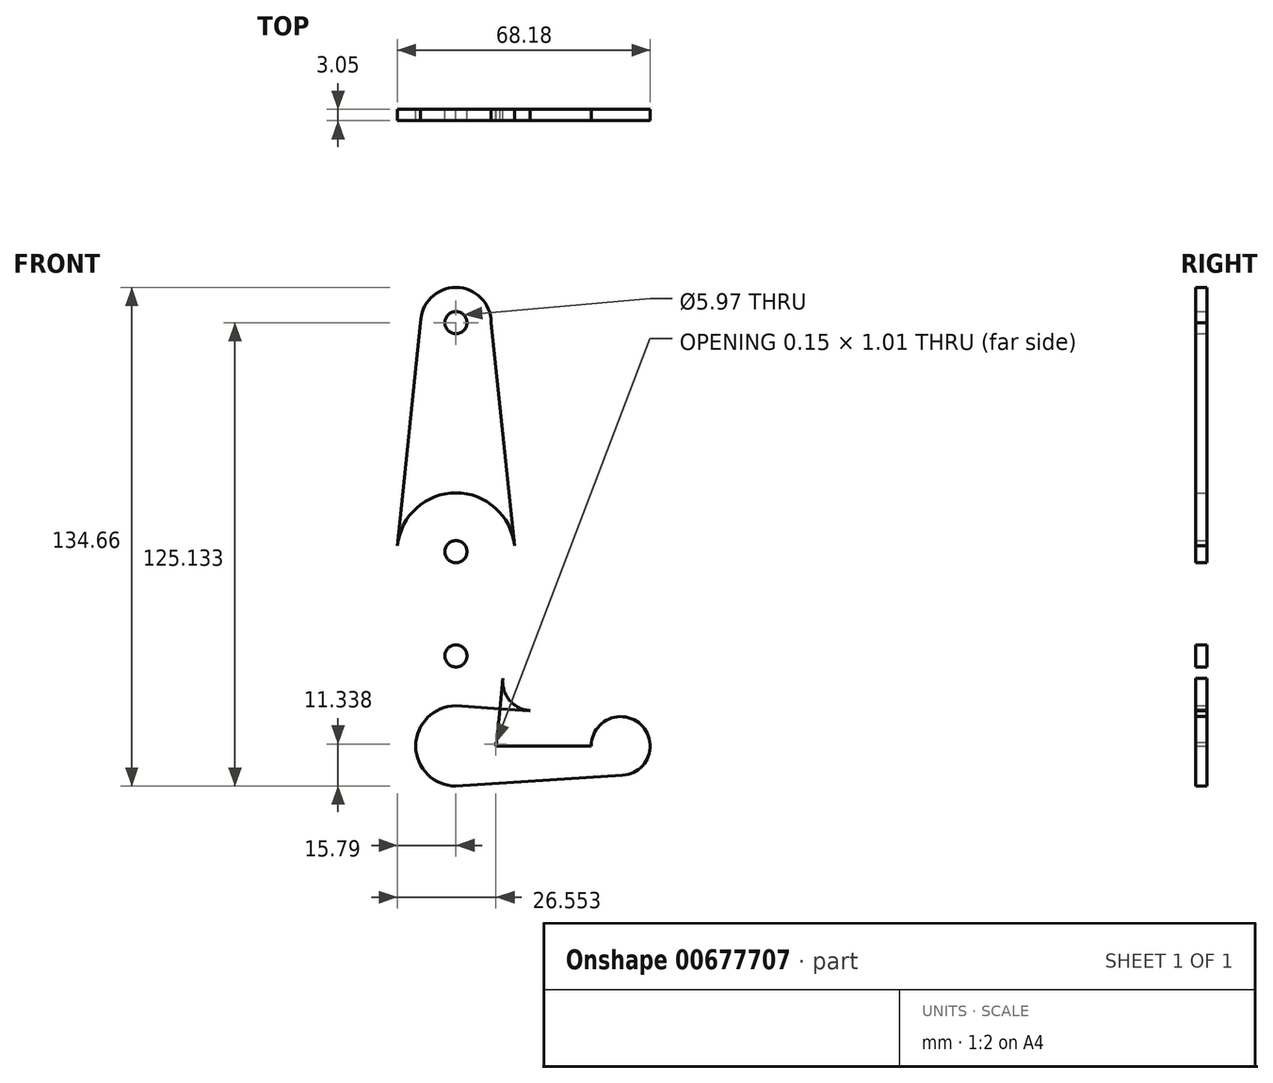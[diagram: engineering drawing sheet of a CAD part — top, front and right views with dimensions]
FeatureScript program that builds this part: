
annotation { "Feature Type Name" : "Feature", "Feature Type Description" : "" }
export const myFeature = defineFeature(function(context is Context, id is Id, definition is map)
    precondition{}
    {
        {
            var Q0;
            Q0=qCreatedBy(makeId("Front.planeOp"),FACE);
            var sketch = newSketch(context, id + "F0", { "sketchPlane" : qUnion([Q0])});
            skLineSegment(sketch, "E0", {"start": v(0, 61.82) * mm, "end": v(0, -52.48) * mm});
            skLineSegment(sketch, "E1", {"start": v(0, -52.48) * mm, "end": v(0, 11.02) * mm});
            skPoint(sketch, "E2.end.orphan", {"position": v(54.75, -52.48) * mm});
            skPoint(sketch, "E3.orphan", {"position": v(35.11, -52.48) * mm});
            skPoint(sketch, "E4.end.orphan", {"position": v(17.56, -52.48) * mm});
            skLineSegment(sketch, "E5", {"start": v(0, -52.48) * mm, "end": v(44.45, -52.48) * mm});
            skCircle(sketch, "E6", {"center": v(0, 0) * mm, "radius": 15.88 * mm});
            skCircle(sketch, "E7", {"center": v(0, 61.82) * mm, "radius": 9.53 * mm});
            skCircle(sketch, "E8", {"center": v(44.45, -52.48) * mm, "radius": 7.94 * mm});
            skCircle(sketch, "E9", {"center": v(0, -52.48) * mm, "radius": 10.84 * mm});
            skLineSegment(sketch, "E10", {"start": v(-15.96, 0) * mm, "end": v(-15.79, -1.66) * mm});
            skLineSegment(sketch, "E11", {"start": v(0, -41.64) * mm, "end": v(44.96, -44.56) * mm});
            skLineSegment(sketch, "E12", {"start": v(0, -63.31) * mm, "end": v(44.96, -60.4) * mm});
            skLineSegment(sketch, "E13", {"start": v(0, 61.82) * mm, "end": v(-9.53, 61.82) * mm});
            skLineSegment(sketch, "E14", {"start": v(-9.53, 61.82) * mm, "end": v(-15.79, 1.64) * mm});
            skLineSegment(sketch, "E15.trimOffspring", {"start": v(10.8, -51.47) * mm, "end": v(10.69, -52.48) * mm});
            skPoint(sketch, "E16.trimOffspring.end.orphan", {"position": v(10.69, -50.69) * mm});
            skLineSegment(sketch, "E17", {"start": v(9.53, 61.82) * mm, "end": v(15.79, 1.64) * mm});
            skPoint(sketch, "E18.trimOffspring.end.orphan", {"position": v(10.8, -49.71) * mm});
            skPoint(sketch, "E19.end.orphan", {"position": v(17.76, 0) * mm});
            skLineSegment(sketch, "E20", {"start": v(15.88, 0) * mm, "end": v(10.89, -52.48) * mm});
            skLineSegment(sketch, "E21", {"start": v(-15.96, 0) * mm, "end": v(-10.65, -50.46) * mm});
            skCircle(sketch, "E22", {"center": v(0, 40.81) * mm, "radius": 2.98 * mm});
            skCircle(sketch, "E23", {"center": v(0, 0) * mm, "radius": 2.98 * mm});
            skCircle(sketch, "E24", {"center": v(0, 61.82) * mm, "radius": 2.98 * mm});
            skCircle(sketch, "E25", {"center": v(0, -28.15) * mm, "radius": 2.98 * mm});
            skLineSegment(sketch, "E26", {"start": v(44.96, -44.56) * mm, "end": v(20.02, -42.94) * mm});
            skLineSegment(sketch, "E27", {"start": v(12.62, -34.25) * mm, "end": v(15.88, 0) * mm});
            skPoint(sketch, "E28.visualSharp", {"position": v(11.84, -42.4) * mm});
            skArc(sketch, "E28.filletArc", {"start": v(12.62, -34.25) * mm, "mid": v(14.48, -40.16) * mm, "end": v(20.02, -42.94) * mm});
            skSolve(sketch);
        }
        {
            var Q0;
            {var subQ0=sQuery(id+"F0.wireOp",EDGE,"E27");var subQ1=sQuery(id+"F0.wireOp",EDGE,"E6");var subQ2=makeQuery(id+"F0.imprint","INTERSECT",VERTEX,{"disambiguationData":[OD(0.0)],"derivedFrom":[subQ1,subQ0]});Q0=makeQuery(id+"F0.imprint","IMPRINT",FACE,{"disambiguationData":[TD([[makeQuery(id+"F0.imprint","IMPRINT",EDGE,{"disambiguationData":[TD([[subQ2,1.0]])],"derivedFrom":subQ1}),1.0]])]});}
            var Q1;
            {var subQ0=sQuery(id+"F0.wireOp",EDGE,"E12");var subQ1=sQuery(id+"F0.wireOp",EDGE,"E9");var subQ2=makeQuery(id+"F0.imprint","INTERSECT",VERTEX,{"disambiguationData":[OD(0.0)],"derivedFrom":[subQ1,subQ0]});Q1=makeQuery(id+"F0.imprint","IMPRINT",FACE,{"disambiguationData":[TD([[makeQuery(id+"F0.imprint","IMPRINT",EDGE,{"disambiguationData":[TD([[subQ2,-1.0]])],"derivedFrom":subQ1}),1.0]])]});}
            var Q2;
            {var subQ0=sQuery(id+"F0.wireOp",EDGE,"E8");var subQ1=makeQuery(id+"F0.imprint","INTERSECT",VERTEX,{"derivedFrom":[subQ0,sQuery(id+"F0.wireOp",EDGE,"E26")]});Q2=makeQuery(id+"F0.imprint","IMPRINT",FACE,{"disambiguationData":[TD([[makeQuery(id+"F0.imprint","IMPRINT",EDGE,{"disambiguationData":[TD([[subQ1,-1.0]])],"derivedFrom":subQ0}),1.0]])]});}
            var Q3;
            {var subQ0=sQuery(id+"F0.wireOp",EDGE,"E28.filletArc");Q3=makeQuery(id+"F0.imprint","IMPRINT",FACE,{"disambiguationData":[TD([[makeQuery(id+"F0.imprint","IMPRINT",EDGE,{"derivedFrom":subQ0}),-1.0]])]});}
            var Q4;
            {var subQ3=sQuery(id+"F0.wireOp",EDGE,"E24");var subQ6=sQuery(id+"F0.wireOp",EDGE,"E0");var subQ8=makeQuery(id+"F0.imprint","INTERSECT",VERTEX,{"derivedFrom":[subQ6,subQ3]});Q4=makeQuery(id+"F0.imprint","IMPRINT",FACE,{"disambiguationData":[TD([[makeQuery(id+"F0.imprint","IMPRINT",EDGE,{"disambiguationData":[TD([[subQ8,-1.0]])],"derivedFrom":subQ6}),1.0]])]});}
            var Q5;
            {var subQ0=sQuery(id+"F0.wireOp",EDGE,"E24");var subQ1=sQuery(id+"F0.wireOp",EDGE,"E0");var subQ2=makeQuery(id+"F0.imprint","INTERSECT",VERTEX,{"derivedFrom":[subQ1,subQ0]});Q5=makeQuery(id+"F0.imprint","IMPRINT",FACE,{"disambiguationData":[TD([[makeQuery(id+"F0.imprint","IMPRINT",EDGE,{"disambiguationData":[TD([[subQ2,-1.0]])],"derivedFrom":subQ1}),-1.0]])]});}
            var Q6;
            {var subQ0=sQuery(id+"F0.wireOp",EDGE,"E17");Q6=makeQuery(id+"F0.imprint","IMPRINT",FACE,{"disambiguationData":[TD([[makeQuery(id+"F0.imprint","IMPRINT",EDGE,{"derivedFrom":subQ0}),-1.0]])]});}
            var Q7;
            {var subQ0=sQuery(id+"F0.wireOp",EDGE,"E14");Q7=makeQuery(id+"F0.imprint","IMPRINT",FACE,{"disambiguationData":[TD([[makeQuery(id+"F0.imprint","IMPRINT",EDGE,{"derivedFrom":subQ0}),1.0]])]});}
            var Q8;
            {var subQ2=sQuery(id+"F0.wireOp",EDGE,"E0");var subQ5=sQuery(id+"F0.wireOp",EDGE,"E1");var subQ8=makeQuery(id+"F0.imprint","INTERSECT",VERTEX,{"derivedFrom":[subQ2,subQ5]});Q8=makeQuery(id+"F0.imprint","IMPRINT",FACE,{"disambiguationData":[TD([[makeQuery(id+"F0.imprint","IMPRINT",EDGE,{"disambiguationData":[TD([[subQ8,1.0]])],"derivedFrom":subQ2}),-1.0]])]});}
            var Q9;
            {var subQ1=sQuery(id+"F0.wireOp",EDGE,"E1");var subQ8=sQuery(id+"F0.wireOp",EDGE,"E25");var subQ9=makeQuery(id+"F0.imprint","INTERSECT",VERTEX,{"disambiguationData":[OD(1.0)],"derivedFrom":[subQ1,subQ8]});Q9=makeQuery(id+"F0.imprint","IMPRINT",FACE,{"disambiguationData":[TD([[makeQuery(id+"F0.imprint","IMPRINT",EDGE,{"disambiguationData":[TD([[subQ9,-1.0]])],"derivedFrom":subQ1}),1.0]])]});}
            var Q10;
            {var subQ3=sQuery(id+"F0.wireOp",EDGE,"E5");var subQ8=makeQuery(id+"F0.imprint","INTERSECT",VERTEX,{"derivedFrom":[subQ3,sQuery(id+"F0.wireOp",EDGE,"E20")]});Q10=makeQuery(id+"F0.imprint","IMPRINT",FACE,{"disambiguationData":[TD([[makeQuery(id+"F0.imprint","IMPRINT",EDGE,{"disambiguationData":[TD([[subQ8,1.0]])],"derivedFrom":subQ3}),-1.0]])]});}
            var Q11;
            {var subQ4=sQuery(id+"F0.wireOp",EDGE,"E1");var subQ5=sQuery(id+"F0.wireOp",EDGE,"E0");var subQ6=makeQuery(id+"F0.imprint","INTERSECT",VERTEX,{"derivedFrom":[subQ5,subQ4]});Q11=makeQuery(id+"F0.imprint","IMPRINT",FACE,{"disambiguationData":[TD([[makeQuery(id+"F0.imprint","IMPRINT",EDGE,{"disambiguationData":[TD([[subQ6,1.0]])],"derivedFrom":subQ5}),1.0]])]});}
            var Q12;
            {var subQ0=sQuery(id+"F0.wireOp",EDGE,"E5");var subQ6=sQuery(id+"F0.wireOp",EDGE,"E1");var subQ9=makeQuery(id+"F0.imprint","INTERSECT",VERTEX,{"derivedFrom":[subQ6,subQ0]});Q12=makeQuery(id+"F0.imprint","IMPRINT",FACE,{"disambiguationData":[TD([[makeQuery(id+"F0.imprint","IMPRINT",EDGE,{"disambiguationData":[TD([[subQ9,-1.0]])],"derivedFrom":subQ0}),-1.0]])]});}
            var Q13;
            {var subQ5=sQuery(id+"F0.wireOp",EDGE,"E26");Q13=makeQuery(id+"F0.imprint","IMPRINT",FACE,{"disambiguationData":[TD([[makeQuery(id+"F0.imprint","IMPRINT",EDGE,{"derivedFrom":subQ5}),1.0]])]});}
            var Q14;
            {var subQ3=sQuery(id+"F0.wireOp",EDGE,"E20");var subQ6=sQuery(id+"F0.wireOp",EDGE,"E5");var subQ8=makeQuery(id+"F0.imprint","INTERSECT",VERTEX,{"derivedFrom":[subQ6,subQ3]});Q14=makeQuery(id+"F0.imprint","IMPRINT",FACE,{"disambiguationData":[TD([[makeQuery(id+"F0.imprint","IMPRINT",EDGE,{"disambiguationData":[TD([[subQ8,1.0]])],"derivedFrom":subQ6}),1.0]])]});}
            var Q15;
            {var subQ7=sQuery(id+"F0.wireOp",EDGE,"E15.trimOffspring");Q15=makeQuery(id+"F0.imprint","IMPRINT",FACE,{"disambiguationData":[TD([[makeQuery(id+"F0.imprint","IMPRINT",EDGE,{"derivedFrom":subQ7}),-1.0]])]});}
            var Q16;
            {var subQ0=sQuery(id+"F0.wireOp",EDGE,"E25");var subQ1=sQuery(id+"F0.wireOp",EDGE,"E1");var subQ2=makeQuery(id+"F0.imprint","INTERSECT",VERTEX,{"disambiguationData":[OD(1.0)],"derivedFrom":[subQ1,subQ0]});Q16=makeQuery(id+"F0.imprint","IMPRINT",FACE,{"disambiguationData":[TD([[makeQuery(id+"F0.imprint","IMPRINT",EDGE,{"disambiguationData":[TD([[subQ2,-1.0]])],"derivedFrom":subQ1}),-1.0]])]});}
            extrude(context, id + "F1", {"entities" : qUnion([Q0, Q1, Q2, Q3, Q4, Q5, Q6, Q7, Q8, Q9, Q10, Q11, Q12, Q13, Q14, Q15, Q16]), "depth" : 3.05 * mm, "offsetDistance" : 25.4 * mm});
        }
    });
